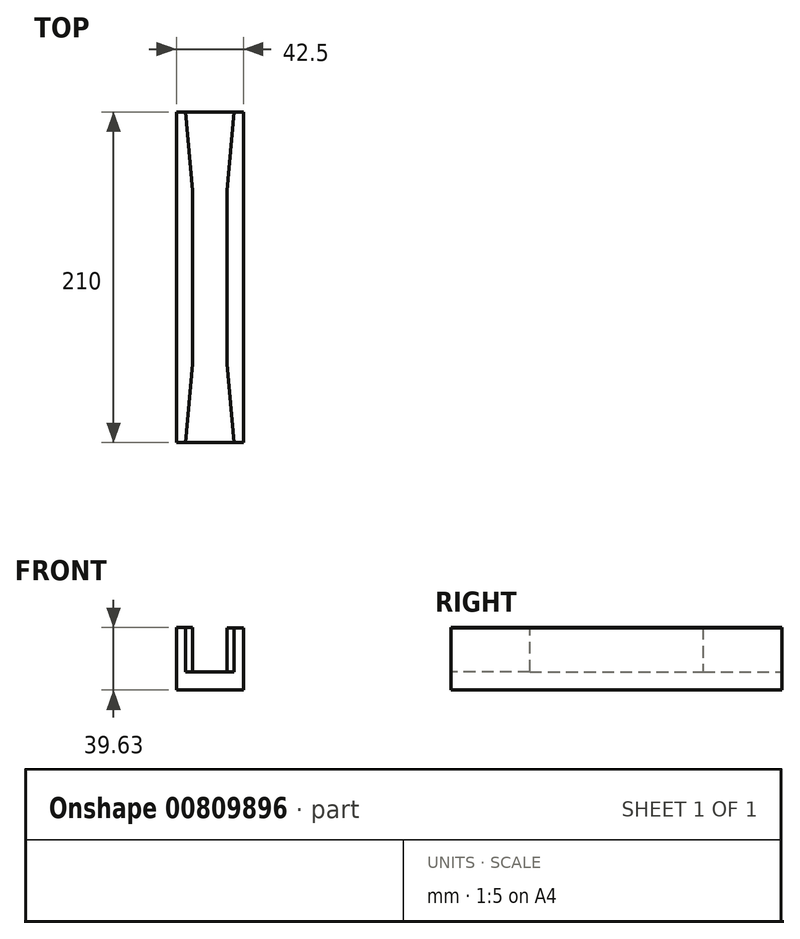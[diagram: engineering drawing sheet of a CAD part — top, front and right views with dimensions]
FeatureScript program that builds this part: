
annotation { "Feature Type Name" : "Feature", "Feature Type Description" : "" }
export const myFeature = defineFeature(function(context is Context, id is Id, definition is map)
    precondition{}
    {
        {
            var Q0;
            Q0=qCreatedBy(makeId("Front.planeOp"),FACE);
            var sketch = newSketch(context, id + "F0", { "sketchPlane" : qUnion([Q0])});
            skLineSegment(sketch, "E0", {"start": v(-21.25, 28) * mm, "end": v(-21.25, -11.63) * mm});
            skLineSegment(sketch, "E1", {"start": v(-21.25, -11.63) * mm, "end": v(21.25, -11.63) * mm});
            skLineSegment(sketch, "E2", {"start": v(21.25, -11.63) * mm, "end": v(21.25, 27.87) * mm});
            skLineSegment(sketch, "E3", {"start": v(21.25, 27.87) * mm, "end": v(11, 27.87) * mm});
            skLineSegment(sketch, "E4", {"start": v(11, 27.87) * mm, "end": v(11, 0) * mm});
            skLineSegment(sketch, "E5", {"start": v(11, 0) * mm, "end": v(-11, 0) * mm});
            skLineSegment(sketch, "E6", {"start": v(-11, 0) * mm, "end": v(-11, 28) * mm});
            skLineSegment(sketch, "E7", {"start": v(-11, 28) * mm, "end": v(-21.25, 28) * mm});
            skPoint(sketch, "E8", {"position": v(0, 10.26) * mm});
            skSolve(sketch);
        }
        {
            var Q0;
            Q0=makeQuery(id+"F0.imprint","IMPRINT",FACE,{"disambiguationData":[TD([[makeQuery(id+"F0.imprint","IMPRINT",EDGE,{"derivedFrom":sQuery(id+"F0.wireOp",EDGE,"E0")}),1.0]])]});
            var Q1;
            Q1 = qSketchRegion(id + "F0", true);
            extrude(context, id + "F1", {"entities" : qUnion([Q0, Q1]), "endBound" : BoundingType.SYMMETRIC, "depth" : 210 * mm, "offsetDistance" : 25 * mm});
        }
        {
            var Q0;
            Q0=makeQuery(id+"F1.opExtrude","CAP_EDGE",EDGE,{"disambiguationData":[OSD([sQuery(id+"F0.wireOp",EDGE,"E6")])],"isStart":false});
            var Q1;
            Q1=makeQuery(id+"F1.opExtrude","CAP_EDGE",EDGE,{"disambiguationData":[OSD([sQuery(id+"F0.wireOp",EDGE,"E4")])],"isStart":false});
            var Q2;
            Q2=makeQuery(id+"F1.opExtrude","CAP_EDGE",EDGE,{"disambiguationData":[OSD([sQuery(id+"F0.wireOp",EDGE,"E6")])],"isStart":true});
            chamfer(context, id + "F2", {"entities" : qUnion([Q0, Q1, Q2]), "chamferType" : ChamferType.OFFSET_ANGLE, "width" : 50 * mm, "oppositeDirection" : true, "angle" : 5 * degree});
        }
        {
            var Q0;
            Q0=makeQuery(id+"F1.opExtrude","CAP_EDGE",EDGE,{"disambiguationData":[OSD([sQuery(id+"F0.wireOp",EDGE,"E4")])],"isStart":true});
            chamfer(context, id + "F3", {"entities" : qUnion([Q0]), "chamferType" : ChamferType.OFFSET_ANGLE, "width" : 50 * mm, "oppositeDirection" : false, "angle" : 5 * degree, "tangentPropagation" : true});
        }
    });
